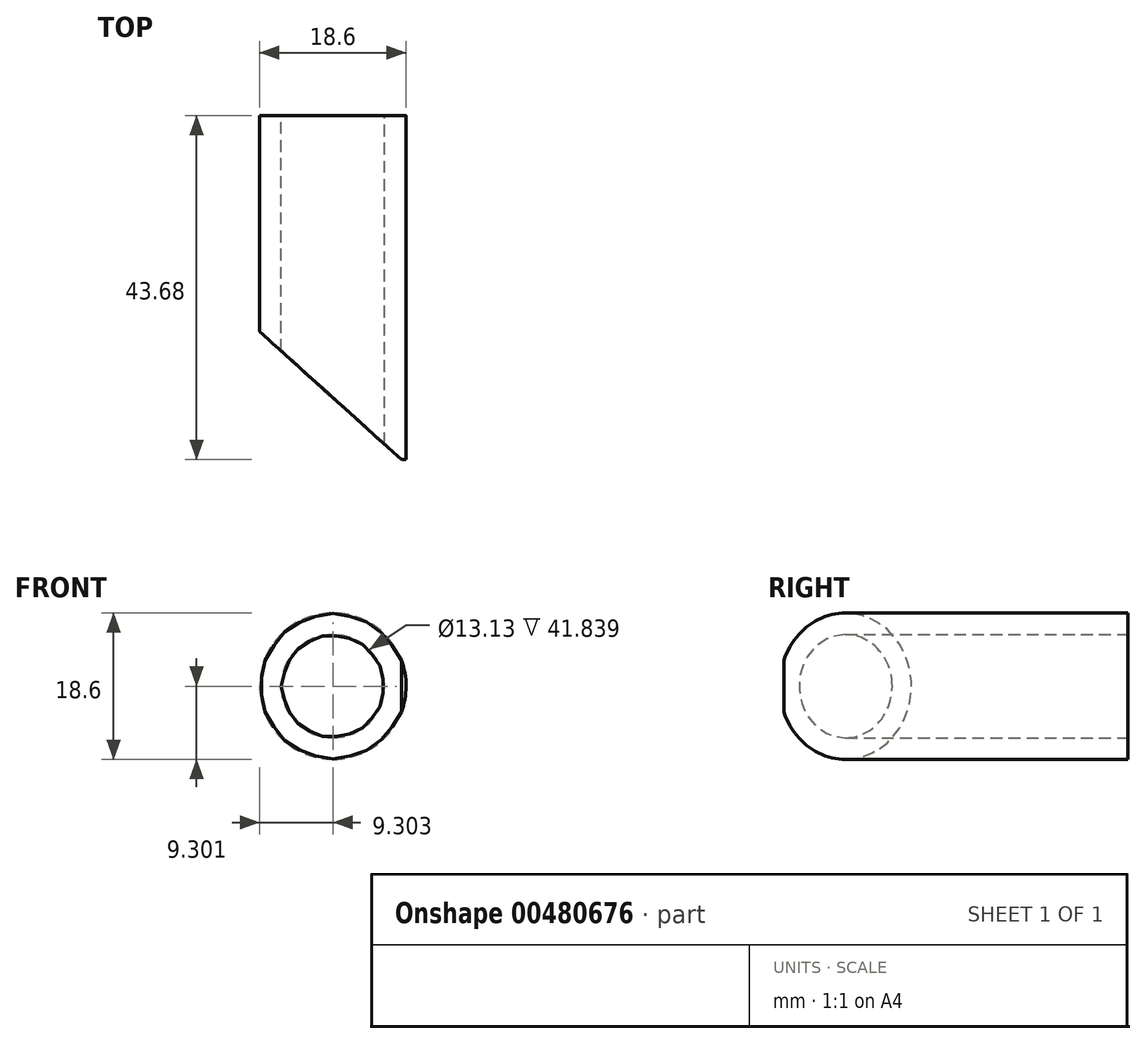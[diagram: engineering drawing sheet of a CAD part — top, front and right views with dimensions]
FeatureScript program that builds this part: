
annotation { "Feature Type Name" : "Feature", "Feature Type Description" : "" }
export const myFeature = defineFeature(function(context is Context, id is Id, definition is map)
    precondition{}
    {
        {
            var Q0;
            Q0=qCreatedBy(makeId("Front.planeOp"),FACE);
            var sketch = newSketch(context, id + "F0", { "sketchPlane" : qUnion([Q0])});
            skCircle(sketch, "E0", {"center": v(-16.84, 12.95) * mm, "radius": 9.3 * mm});
            skCircle(sketch, "E1", {"center": v(-16.84, 12.95) * mm, "radius": 6.56 * mm});
            skSolve(sketch);
        }
        {
            var Q0;
            Q0=qSketchRegion(id+"F0",true);
            extrude(context, id + "F1", {"entities" : qUnion([Q0]), "endBound" : BoundingType.SYMMETRIC, "depth" : 43.69 * mm});
        }
        {
            var Q0;
            Q0=qCreatedBy(makeId("Top.planeOp"),FACE);
            var sketch = newSketch(context, id + "F2", { "sketchPlane" : qUnion([Q0])});
            skLineSegment(sketch, "E2", {"start": v(0, -29.19) * mm, "end": v(-33.08, -29.19) * mm});
            skLineSegment(sketch, "E3", {"start": v(-33.08, -29.19) * mm, "end": v(-33.08, 0.67) * mm});
            skLineSegment(sketch, "E4", {"start": v(-33.08, 0.67) * mm, "end": v(0, -29.19) * mm});
            skSolve(sketch);
        }
        {
            var Q0;
            Q0=qSketchRegion(id+"F2",true);
            extrude(context, id + "F3", {"entities" : qUnion([Q0]), "operationType" : NewBodyOperationType.REMOVE, "depth" : 25.4 * mm});
        }
    });
